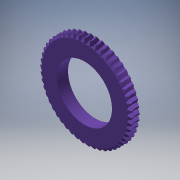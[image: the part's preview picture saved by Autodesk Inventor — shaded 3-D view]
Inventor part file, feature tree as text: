
AUTODESK INVENTOR PART (.ipt)
format: ipt  version: 2019.3 (Build 233278000, 278)  size: 1,015,808 bytes
history: native  units: mm (DEFAULTED — no unit token found)
features: other x8, plane x3, sketch x2, pattern_circular x1, extrude x1
ambient origin geometry x5: Origin, X Axis, Y Axis, Z Axis, Center Point
bodies: Solid1 (feature_tree)
feature tree (15):
  other  "Tooth Plane"
  other  "Base Body Sketch"
  other  "Base Body"
  other  "Base Body2"
  plane  "Work Plane13"
  other  "Tooth"
  pattern_circular  "Tooth Pattern"  [2 undecoded]
  plane  "Work Plane14"
  plane  "Work Plane15"
  extrude  "Extrusion1"  Depth=48.510427mm
  other  "Tooth Sketch"
  sketch  "Sketch8"  dims[d35=90.0deg]
  other  "Srf1"
  sketch  "Sketch9"  dims[d37=-0.996687mm d38=48.510427mm d39=3.490659mm d40=6.144654mm d41=8.085071mm d42=1.524mm d43=90.0deg d44=500.0mm d46=360.0deg d50=5.510696mm d68=48.510427mm d69=0.0mm d73=0.0mm d75=0.628319mm d77=80.850711mm d78=10.16mm d79=0.0mm d80=0.0mm d81=0.0mm d82=0.0mm d83=0.628319mm d84=0.0mm d85=180.0deg d86=48.510427mm d87=85.701754mm d89=12.936114mm d90=90.0deg d92=10.16mm d93=48.510427mm d94=51.308mm d95=25.4mm d96=0.0mm]
  other  "Pitch Diameter"
note: 2 required parameter values undecoded (feature->parameter linkage not recoverable at this tier; creation-order binding heuristic only, values carry confidence <= 0.55)
